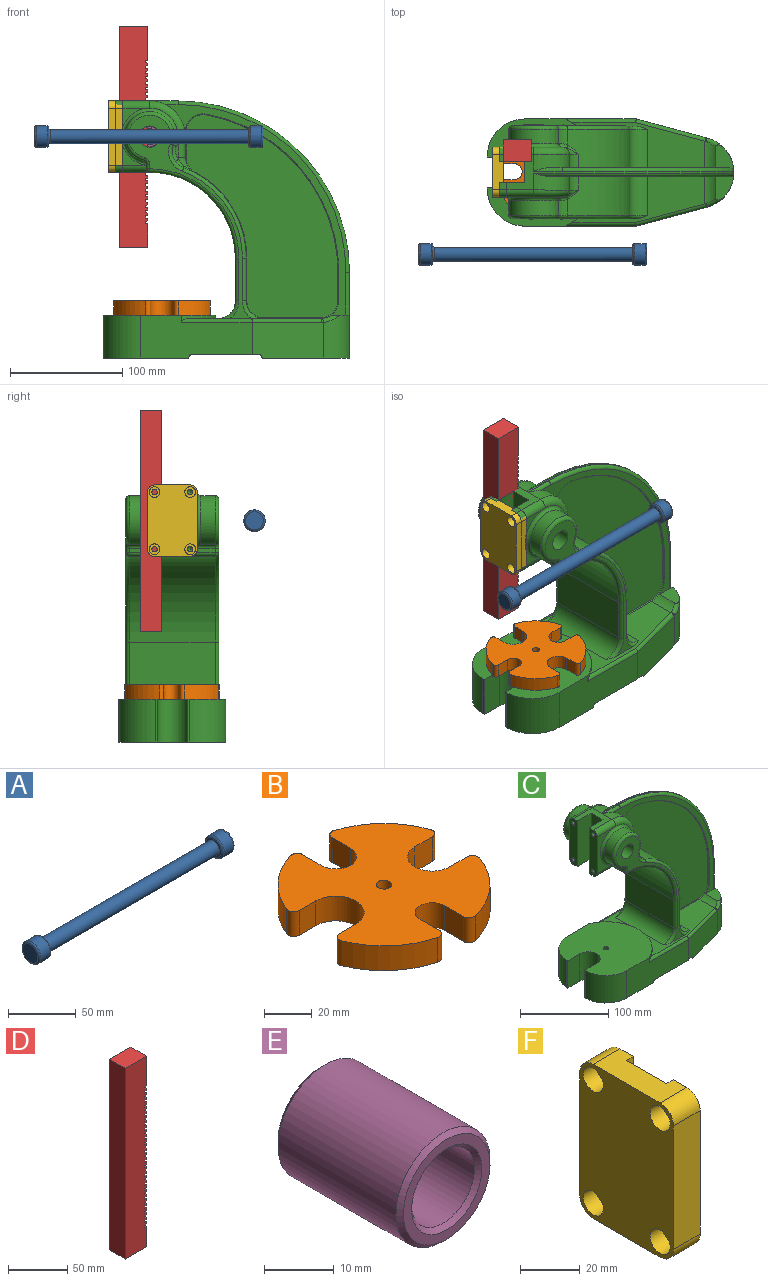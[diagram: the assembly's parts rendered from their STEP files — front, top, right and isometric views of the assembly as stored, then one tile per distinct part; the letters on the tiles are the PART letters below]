
ASSEMBLY  parts=6 mates=1
PART A: 12 faces, bbox 203.2x20.6x20.6 mm
  f0: cylinder r=6.1mm len=176.28mm, axis (-1,0,0), area 6751.8mm2, adj f5,f7
  f1: cylinder r=9.53mm len=19.05mm, axis (-1,0,0), area 577.6mm2, adj f10,f11
  f2: plane 16x16mm, normal (1,0,0), area 18.7mm2, adj f7,f11
  f3: plane 16x16mm, normal (-1,0,0), area 201.1mm2, adj f10
  f4: cylinder r=9.53mm len=19.05mm, axis (1,0,0), area 577.6mm2, adj f8,f9
  f5: plane 16x16mm, normal (-1,0,0), area 84.4mm2, adj f0,f9
  f6: plane 16x16mm, normal (1,0,0), area 201.1mm2, adj f8
  f7: torus R=7.62mm, axis (-1,0,0), area 100mm2, adj f0,f2
  f8: torus R=8mm, axis (1,0,0), area 134.9mm2, adj f4,f6
  f9: torus R=8mm, axis (1,0,0), area 134.9mm2, adj f4,f5
  f10: torus R=8mm, axis (1,0,0), area 134.9mm2, adj f1,f3
  f11: torus R=8mm, axis (-1,0,0), area 134.9mm2, adj f1,f2
PART B: 27 faces, bbox 83.8x85.8x12.7 mm
  f0: cylinder r=44.45mm len=28.56mm, axis (0,0,-1), area 510.6mm2, adj f17,f18,f19,f25
  f1: plane 12.7x9.85mm, normal (0,-1,0), area 125.1mm2, adj f2,f17,f18,f25
  f2: cylinder r=11.9mm len=23.8mm, axis (0,0,-1), area 474.8mm2, adj f1,f3,f17,f18
  f3: plane 12.7x9.85mm, normal (0,1,0), area 125.1mm2, adj f2,f17,f18,f26
  f4: cylinder r=44.45mm len=30.27mm, axis (0,0,-1), area 533.1mm2, adj f17,f18,f20,f26
  f5: plane 12.7x11.39mm, normal (1,0,0), area 144.7mm2, adj f6,f17,f18,f20
  f6: cylinder r=7.14mm len=14.28mm, axis (0,0,-1), area 284.8mm2, adj f5,f7,f17,f18
  f7: plane 12.7x11.39mm, normal (-1,0,0), area 144.7mm2, adj f6,f17,f18,f21
  f8: cylinder r=44.45mm len=30.9mm, axis (0,0,-1), area 556.3mm2, adj f17,f18,f21,f22
  f9: plane 12.7x10.43mm, normal (0,1,0), area 132.5mm2, adj f10,f17,f18,f22
  f10: cylinder r=10.31mm len=20.62mm, axis (0,0,-1), area 411.4mm2, adj f9,f11,f17,f18
  f11: plane 12.7x10.43mm, normal (0,-1,0), area 132.5mm2, adj f10,f17,f18,f23
  f12: cylinder r=44.45mm len=29.19mm, axis (0,0,-1), area 533.7mm2, adj f17,f18,f23,f24
  f13: plane 12.7x10.95mm, normal (-1,0,0), area 139mm2, adj f14,f17,f18,f24
  f14: cylinder r=8.72mm len=17.45mm, axis (0,0,-1), area 348.1mm2, adj f13,f15,f17,f18
  f15: plane 12.7x10.95mm, normal (1,0,0), area 139mm2, adj f14,f17,f18,f19
  f16: cylinder r=3.17mm len=12.7mm, axis (0,0,-1), area 253.4mm2, adj f17,f18
  f17: plane 85.84x83.78mm, normal (0,0,1), area 4373.8mm2, adj f0,f1,f2,f3,f4,f5,f6,f7
  f18: plane 85.84x83.78mm, normal (0,0,-1), area 4373.8mm2, adj f0,f1,f2,f3,f4,f5,f6,f7
  f19: cylinder r=3.17mm len=12.7mm, axis (0,0,-1), area 75.1mm2, adj f0,f15,f17,f18
  f20: cylinder r=3.17mm len=12.7mm, axis (0,0,-1), area 73.5mm2, adj f4,f5,f17,f18
  f21: cylinder r=3.17mm len=12.7mm, axis (0,0,-1), area 73.5mm2, adj f7,f8,f17,f18
  f22: cylinder r=3.17mm len=12.7mm, axis (0,0,-1), area 76.8mm2, adj f8,f9,f17,f18
  f23: cylinder r=3.17mm len=12.7mm, axis (0,0,-1), area 76.8mm2, adj f11,f12,f17,f18
  f24: cylinder r=3.17mm len=12.7mm, axis (0,0,-1), area 75.1mm2, adj f12,f13,f17,f18
  f25: cylinder r=3.17mm len=12.7mm, axis (0,0,-1), area 78.4mm2, adj f0,f1,f17,f18
  f26: cylinder r=3.17mm len=12.7mm, axis (0,0,-1), area 78.4mm2, adj f3,f4,f17,f18
PART C: 180 faces, bbox 234.5x98.1x244 mm
  f0: plane 63.5x12.7mm, normal (-1,0,0), area 753.5mm2, adj f2,f15,f17,f92,f97,f149,f151,f158
  f1: plane 20.23x2.34mm, normal (0,1,0), area 23.9mm2, adj f90,f91,f104,f106
  f2: plane 50.8x30.1mm, normal (0,-1,0), area 515.4mm2, adj f0,f83,f92,f97,f124
  f3: plane 22.59x12.73mm, normal (1,0,0), area 235.4mm2, adj f19,f26,f32,f87,f94,f174
  f4: plane 22.59x12.73mm, normal (1,0,0), area 235.4mm2, adj f10,f14,f33,f86,f90,f164
  f5: plane 99.19x38.1mm, normal (0,-1,0), area 3202mm2, adj f6,f40,f46,f49,f52,f58,f76,f133
  f6: plane 100x95.25mm, normal (0,0,1), area 7398mm2, adj f5,f43,f44,f48,f54,f55,f56,f57
  f7: plane 38.1x34.96mm, normal (1,0,0), area 1331.9mm2, adj f8,f9,f114,f169
  f8: cylinder r=15.88mm len=34.96mm, axis (0,1,0), area 871.7mm2, adj f7,f37,f115,f167
  f9: cylinder r=85.72mm len=80.21mm, axis (0,1,0), area 3442.3mm2, adj f7,f80,f86,f100,f113,f168
  f10: cylinder r=15.88mm len=18.65mm, axis (0,1,0), area 22.7mm2, adj f4,f11,f33,f162
  f11: cylinder r=142.88mm len=140.67mm, axis (0,1,0), area 163.3mm2, adj f10,f12,f33,f160
  f12: plane 25.4x0.82mm, normal (-1,0,0), area 20.8mm2, adj f11,f13,f33,f161
  f13: cylinder r=15.88mm len=24.81mm, axis (0,1,0), area 242.1mm2, adj f12,f33,f37,f45,f139,f140,f163
  f14: cylinder r=31.75mm len=31.75mm, axis (0,1,0), area 616.8mm2, adj f4,f15,f33,f89,f141
  f15: plane 55.5x31.75mm, normal (0,0,1), area 573.2mm2, adj f0,f14,f16,f19,f31,f88,f92,f141
  f16: plane 63.5x12.7mm, normal (-1,0,0), area 753.5mm2, adj f15,f17,f21,f88,f96,f147,f153,f157
  f17: plane 31.75x30.1mm, normal (0,0,-1), area 533.2mm2, adj f0,f16,f18,f96,f97,f156,f157,f158
  f18: cylinder r=76.2mm len=76.2mm, axis (0,1,0), area 9120.7mm2, adj f17,f22,f103,f105,f119,f121
  f19: cylinder r=31.75mm len=31.75mm, axis (0,1,0), area 616.8mm2, adj f3,f15,f32,f93,f144
  f20: plane 20.23x2.34mm, normal (0,-1,0), area 23.9mm2, adj f94,f95,f122,f124
  f21: plane 50.8x30.1mm, normal (0,1,0), area 515.4mm2, adj f16,f78,f88,f96,f106
  f22: plane 76.2x38.1mm, normal (-1,0,0), area 2903.2mm2, adj f18,f98,f101,f117
  f23: cylinder r=15.88mm len=34.96mm, axis (0,1,0), area 871.7mm2, adj f24,f37,f132,f177
  f24: plane 38.1x34.96mm, normal (1,0,0), area 1331.9mm2, adj f23,f25,f131,f179
  f25: cylinder r=85.72mm len=80.21mm, axis (0,1,0), area 3442.3mm2, adj f24,f81,f87,f118,f130,f178
  f26: cylinder r=15.88mm len=18.65mm, axis (0,1,0), area 22.7mm2, adj f3,f27,f32,f172
  f27: cylinder r=142.88mm len=140.67mm, axis (0,1,0), area 163.3mm2, adj f26,f28,f32,f170
  f28: plane 25.4x0.82mm, normal (-1,0,0), area 20.8mm2, adj f27,f29,f32,f171
  f29: cylinder r=15.88mm len=24.81mm, axis (0,1,0), area 242.1mm2, adj f28,f32,f36,f37,f135,f136,f173
  f30: plane 76.2x7.92mm, normal (1,0,0), area 361.9mm2, adj f31,f36,f42,f45,f51,f53,f143,f146
  f31: cylinder r=152.4mm len=152.4mm, axis (0,1,0), area 377mm2, adj f15,f30,f142,f145
  f32: plane 187.33x160.79mm, normal (0,-1,0), area 1900.4mm2, adj f3,f19,f26,f27,f28,f29,f36,f144
  f33: plane 187.33x160.79mm, normal (0,1,0), area 1900.4mm2, adj f4,f10,f11,f12,f13,f14,f45,f141
  f34: plane 180.67x135mm, normal (0,-1,0), area 14138.8mm2, adj f170,f171,f172,f173,f174,f175,f176,f177
  f35: plane 180.67x135mm, normal (0,1,0), area 14138.8mm2, adj f160,f161,f162,f163,f164,f165,f166,f167
  f36: plane 26.58x18.73mm, normal (0,0,1), area 245.8mm2, adj f29,f30,f32,f53,f136,f146
  f37: plane 119.12x89.67mm, normal (0,0,1), area 4280.2mm2, adj f8,f13,f23,f29,f76,f77,f84,f98
  f38: cylinder r=3.17mm len=9.06mm, axis (0,1,0), area 40.9mm2, adj f40,f42,f52,f69
  f39: cylinder r=3.17mm len=7.93mm, axis (0,1,0), area 39.5mm2, adj f41,f46,f48,f65
  f40: plane 58.73x9.7mm, normal (0,0,-1), area 467.1mm2, adj f5,f38,f49,f52,f64,f69
  f41: plane 58.73x9.7mm, normal (0,0,-1), area 467.1mm2, adj f39,f47,f48,f50,f65,f67
  f42: plane 90.55x77.8mm, normal (0,0,-1), area 1454mm2, adj f30,f38,f47,f50,f51,f52,f53,f59
  f43: plane 38.1x1.61mm, normal (-1,0,0), area 61.5mm2, adj f6,f46,f54,f58
  f44: plane 38.1x1.61mm, normal (-1,0,0), area 61.5mm2, adj f6,f46,f55,f57
  f45: plane 26.58x18.73mm, normal (0,0,1), area 245.8mm2, adj f13,f30,f33,f51,f140,f143
  f46: plane 95.25x76.2mm, normal (0,0,-1), area 2029.8mm2, adj f5,f39,f43,f44,f48,f49,f54,f55
  f47: cylinder r=3.17mm len=9.06mm, axis (0,1,0), area 40.9mm2, adj f41,f42,f50,f67
  f48: plane 99.19x38.1mm, normal (0,1,0), area 3202mm2, adj f6,f39,f41,f46,f50,f57,f76,f137
  f49: cylinder r=3.17mm len=7.93mm, axis (0,1,0), area 39.5mm2, adj f5,f40,f46,f64
  f50: plane 63.64x32.15mm, normal (0.26,0.97,0), area 2053.6mm2, adj f41,f42,f47,f48,f51,f138,f139
  f51: cylinder r=31.75mm len=38.1mm, axis (0,0,-1), area 1379.2mm2, adj f30,f42,f45,f50,f140
  f52: plane 63.64x32.15mm, normal (0.26,-0.97,0), area 2053.6mm2, adj f5,f38,f40,f42,f53,f134,f135
  f53: cylinder r=31.75mm len=38.1mm, axis (0,0,-1), area 1379.2mm2, adj f30,f36,f42,f52,f136
  f54: plane 38.1x19.05mm, normal (0,1,0), area 725.8mm2, adj f6,f43,f46,f56
  f55: plane 38.1x19.05mm, normal (0,-1,0), area 725.8mm2, adj f6,f44,f46,f56
  f56: cylinder r=13.49mm len=38.1mm, axis (0,0,-1), area 1615.1mm2, adj f6,f46,f54,f55
  f57: cylinder r=33.32mm len=38.1mm, axis (0,0,-1), area 1963.7mm2, adj f6,f44,f46,f48
  f58: cylinder r=33.32mm len=38.1mm, axis (0,0,-1), area 1963.7mm2, adj f5,f6,f43,f46
  f59: plane 30.18x6.86mm, normal (-1,0,0), area 207mm2, adj f42,f60,f68,f70
  f60: plane 31.27x5.6mm, normal (0,0,-1), area 124.1mm2, adj f59,f61,f68,f70
  f61: cylinder r=23.8mm len=46.06mm, axis (0,1,0), area 499.2mm2, adj f60,f62,f67,f68,f69,f70
  f62: plane 84.13x79.4mm, normal (0,0,-1), area 5642.5mm2, adj f61,f64,f65,f66,f67,f69
  f63: plane 100.62x79.4mm, normal (0,0,-1), area 6568.5mm2, adj f64,f65,f66,f71,f72,f73,f74,f75
  f64: plane 98.15x30.18mm, normal (0,1,0), area 2718.8mm2, adj f40,f46,f49,f62,f63,f66,f69,f75
  f65: plane 98.15x30.18mm, normal (0,-1,0), area 2718.8mm2, adj f39,f41,f46,f62,f63,f66,f67,f74
  f66: plane 79.4x3.18mm, normal (-1,0,0), area 252.1mm2, adj f62,f63,f64,f65
  f67: plane 62.63x27.36mm, normal (-0.26,-0.97,0), area 1710.8mm2, adj f41,f42,f47,f61,f62,f65,f68
  f68: cylinder r=23.83mm len=30.18mm, axis (0,0,-1), area 814.8mm2, adj f42,f59,f60,f61,f67
  f69: plane 62.63x27.36mm, normal (-0.26,0.97,0), area 1710.8mm2, adj f38,f40,f42,f61,f62,f64,f70
  f70: cylinder r=23.83mm len=30.18mm, axis (0,0,-1), area 814.8mm2, adj f42,f59,f60,f61,f69
  f71: plane 30.18x10.12mm, normal (0,-1,0), area 305.3mm2, adj f46,f63,f73,f75
  f72: plane 30.18x10.12mm, normal (0,1,0), area 305.3mm2, adj f46,f63,f73,f74
  f73: cylinder r=21.42mm len=42.84mm, axis (0,0,-1), area 2030.4mm2, adj f46,f63,f71,f72
  f74: cylinder r=25.4mm len=30.18mm, axis (0,0,-1), area 986.2mm2, adj f46,f63,f65,f72
  f75: cylinder r=25.4mm len=30.18mm, axis (0,0,-1), area 986.2mm2, adj f46,f63,f64,f71
  f76: cylinder r=52.37mm len=95.25mm, axis (0,0,1), area 401mm2, adj f5,f6,f37,f48,f133,f137
  f77: plane 180.98x110.12mm, normal (0,1,0), area 1717.8mm2, adj f37,f85,f99,f101,f103,f109,f110,f111
  f78: plane 16.73x3.98mm, normal (-1,0,0), area 64.1mm2, adj f21,f96,f105,f106,f108,f109
  f79: cylinder r=22.23mm len=44.45mm, axis (0,1,0), area 1356.2mm2, adj f80,f106,f108,f111
  f80: cylinder r=15.88mm len=20.22mm, axis (0,1,0), area 319.4mm2, adj f9,f79,f102,f104,f112
  f81: cylinder r=15.88mm len=20.22mm, axis (0,1,0), area 319.4mm2, adj f25,f82,f120,f122,f129
  f82: cylinder r=22.23mm len=44.45mm, axis (0,1,0), area 1356.2mm2, adj f81,f124,f126,f128
  f83: plane 16.73x3.98mm, normal (-1,0,0), area 64.1mm2, adj f2,f97,f121,f124,f125,f126
  f84: plane 180.98x110.12mm, normal (0,-1,0), area 1717.8mm2, adj f37,f85,f116,f117,f119,f125,f127,f128
  f85: cylinder r=9.53mm len=82.55mm, axis (0,1,0), area 4727mm2, adj f77,f84,f156,f157,f158,f159
  f86: cylinder r=15.88mm len=14.02mm, axis (0,1,0), area 218.9mm2, adj f4,f9,f91,f166
  f87: cylinder r=15.88mm len=14.02mm, axis (0,1,0), area 218.9mm2, adj f3,f25,f95,f176
  f88: cylinder r=6.35mm len=30.1mm, axis (-1,0,0), area 300.2mm2, adj f15,f16,f21,f89
  f89: torus R=25.4mm, axis (0,-1,0), area 461.3mm2, adj f14,f88,f90,f106
  f90: cylinder r=6.35mm len=18.2mm, axis (0,0,1), area 181.6mm2, adj f1,f4,f89,f91
  f91: torus R=22.23mm, axis (0,-1,0), area 98mm2, adj f1,f86,f90,f100,f102
  f92: cylinder r=6.35mm len=30.1mm, axis (1,0,0), area 300.2mm2, adj f0,f2,f15,f93
  f93: torus R=25.4mm, axis (0,-1,0), area 461.3mm2, adj f19,f92,f94,f124
  f94: cylinder r=6.35mm len=18.2mm, axis (0,0,-1), area 181.6mm2, adj f3,f20,f93,f95
  f95: torus R=22.23mm, axis (0,-1,0), area 98mm2, adj f20,f87,f94,f118,f120
  f96: cylinder r=6.35mm len=30.1mm, axis (1,0,0), area 279.1mm2, adj f16,f17,f21,f78,f105
  f97: cylinder r=6.35mm len=30.1mm, axis (-1,0,0), area 279.1mm2, adj f0,f2,f17,f83,f121
  f98: cylinder r=15.88mm len=76.2mm, axis (0,-1,0), area 1900.2mm2, adj f22,f37,f99,f116
  f99: torus R=19.05mm, axis (0,-1,0), area 107.7mm2, adj f37,f77,f98,f101
  f100: bspline ~12.01x8.85mm, area 17.9mm2, adj f9,f91,f102
  f101: cylinder r=3.17mm len=38.1mm, axis (0,0,-1), area 190mm2, adj f22,f77,f99,f103
  f102: bspline ~10.6x9.56mm, area 36.6mm2, adj f80,f91,f100,f104
  f103: torus R=79.38mm, axis (0,-1,0), area 606mm2, adj f18,f77,f101,f107
  f104: torus R=12.7mm, axis (0,-1,0), area 70.6mm2, adj f1,f80,f102,f106
  f105: cylinder r=3.17mm len=22.23mm, axis (0,1,0), area 97.1mm2, adj f18,f78,f96,f107
  f106: torus R=25.4mm, axis (0,-1,0), area 570mm2, adj f1,f21,f78,f79,f89,f104,f108
  f107: sphere r=3.17mm, area 21.6mm2, adj f103,f105,f109
  f108: cylinder r=3.17mm len=15.82mm, axis (0,1,0), area 59.7mm2, adj f78,f79,f106,f110
  f109: cylinder r=3.17mm len=3.98mm, axis (0,0,-1), area 19.9mm2, adj f77,f78,f107,f110
  f110: torus R=6.35mm, axis (0,-1,0), area 28.5mm2, adj f77,f108,f109,f111
  f111: torus R=19.05mm, axis (0,-1,0), area 504.9mm2, adj f77,f79,f110,f112
  f112: torus R=19.05mm, axis (0,-1,0), area 132.1mm2, adj f77,f80,f111,f113
  f113: torus R=82.55mm, axis (0,-1,0), area 510.4mm2, adj f9,f77,f112,f114
  f114: cylinder r=3.17mm len=38.1mm, axis (0,0,1), area 190mm2, adj f7,f77,f113,f115
  f115: torus R=19.05mm, axis (0,-1,0), area 107.7mm2, adj f8,f37,f77,f114
  f116: torus R=19.05mm, axis (0,-1,0), area 107.7mm2, adj f37,f84,f98,f117
  f117: cylinder r=3.17mm len=38.1mm, axis (0,0,1), area 190mm2, adj f22,f84,f116,f119
  f118: bspline ~11.06x8.44mm, area 17.9mm2, adj f25,f95,f120
  f119: torus R=79.38mm, axis (0,-1,0), area 606mm2, adj f18,f84,f117,f123
  f120: bspline ~9.12x8.99mm, area 36.6mm2, adj f81,f95,f118,f122
  f121: cylinder r=3.17mm len=22.23mm, axis (0,1,0), area 97.1mm2, adj f18,f83,f97,f123
  f122: torus R=12.7mm, axis (0,-1,0), area 70.6mm2, adj f20,f81,f120,f124
  f123: sphere r=3.17mm, area 15.8mm2, adj f119,f121,f125
  f124: torus R=25.4mm, axis (0,-1,0), area 570mm2, adj f2,f20,f82,f83,f93,f122,f126
  f125: cylinder r=3.17mm len=3.98mm, axis (0,0,1), area 19.9mm2, adj f83,f84,f123,f127
  f126: cylinder r=3.17mm len=15.82mm, axis (0,1,0), area 59.7mm2, adj f82,f83,f124,f127
  f127: torus R=6.35mm, axis (0,-1,0), area 28.5mm2, adj f84,f125,f126,f128
  f128: torus R=19.05mm, axis (0,-1,0), area 504.9mm2, adj f82,f84,f127,f129
  f129: torus R=19.05mm, axis (0,-1,0), area 132.1mm2, adj f81,f84,f128,f130
  f130: torus R=82.55mm, axis (0,-1,0), area 510.4mm2, adj f25,f84,f129,f131
  f131: cylinder r=3.17mm len=38.1mm, axis (0,0,-1), area 190mm2, adj f24,f84,f130,f132
  f132: torus R=19.05mm, axis (0,-1,0), area 107.7mm2, adj f23,f37,f84,f131
  f133: cylinder r=3.17mm len=63.09mm, axis (1,0,0), area 298.9mm2, adj f5,f37,f76,f134
  f134: cylinder r=3.17mm len=62.81mm, axis (0.97,0.26,0), area 319mm2, adj f37,f52,f133,f135
  f135: bspline ~3.41x3.21mm, area 6mm2, adj f29,f52,f134,f136
  f136: bspline ~18.95x11.92mm, area 79.7mm2, adj f29,f36,f53,f135
  f137: cylinder r=3.17mm len=63.09mm, axis (-1,0,0), area 298.9mm2, adj f37,f48,f76,f138
  f138: cylinder r=3.17mm len=62.81mm, axis (-0.97,0.26,0), area 319mm2, adj f37,f50,f137,f139
  f139: bspline ~6.89x4.84mm, area 6mm2, adj f13,f50,f138,f140
  f140: bspline ~17.46x11.57mm, area 79.7mm2, adj f13,f45,f51,f139
  f141: cylinder r=3.17mm len=25.4mm, axis (-1,0,0), area 92.2mm2, adj f14,f15,f33,f142
  f142: torus R=149.22mm, axis (0,-1,0), area 1184.9mm2, adj f31,f33,f141,f143
  f143: cylinder r=3.17mm len=38.1mm, axis (0,0,1), area 190mm2, adj f30,f33,f45,f142
  f144: cylinder r=3.17mm len=25.4mm, axis (1,0,0), area 92.2mm2, adj f15,f19,f32,f145
  f145: torus R=149.22mm, axis (0,-1,0), area 1184.9mm2, adj f31,f32,f144,f146
  f146: cylinder r=3.17mm len=38.1mm, axis (0,0,-1), area 190mm2, adj f30,f32,f36,f145
  f147: cylinder r=2.38mm len=6.35mm, axis (-1,0,0), area 95mm2, adj f16,f148
  f148: cone r=0mm half-angle=59deg, axis (-1,0,0), area 20.8mm2, adj f147
  f149: cylinder r=2.38mm len=6.35mm, axis (-1,0,0), area 95mm2, adj f0,f150
  f150: cone r=0mm half-angle=59deg, axis (-1,0,0), area 20.8mm2, adj f149
  f151: cylinder r=2.38mm len=6.35mm, axis (-1,0,0), area 95mm2, adj f0,f152
  f152: cone r=0mm half-angle=59deg, axis (-1,0,0), area 20.8mm2, adj f151
  f153: cylinder r=2.38mm len=6.35mm, axis (-1,0,0), area 95mm2, adj f16,f154
  f154: cone r=0mm half-angle=59deg, axis (-1,0,0), area 20.8mm2, adj f153
  f155: cylinder r=3.17mm len=7.93mm, axis (0,0,1), area 158.1mm2, adj f6,f63
  f156: plane 26.47x19.05mm, normal (-1,0,0), area 504.2mm2, adj f17,f85,f157,f158
  f157: plane 63.5x22.17mm, normal (0,-1,0), area 1396.6mm2, adj f15,f16,f17,f85,f156,f159
  f158: plane 63.5x22.17mm, normal (0,1,0), area 1396.6mm2, adj f0,f15,f17,f85,f156,f159
  f159: plane 26.47x19.05mm, normal (-1,0,0), area 504.2mm2, adj f15,f85,f157,f158
  f160: torus R=142.11mm, axis (0,-1,0), area 238.1mm2, adj f11,f35,f161,f162
  f161: cylinder r=0.76mm len=25.4mm, axis (0,0,1), area 30.4mm2, adj f12,f35,f160,f163
  f162: torus R=15.11mm, axis (0,-1,0), area 32.6mm2, adj f10,f35,f160,f164
  f163: torus R=15.11mm, axis (0,-1,0), area 29.3mm2, adj f13,f35,f161,f165
  f164: cylinder r=0.76mm len=22.59mm, axis (0,0,1), area 27mm2, adj f4,f35,f162,f166
  f165: cylinder r=0.76mm len=50.8mm, axis (1,0,0), area 60.8mm2, adj f35,f37,f163,f167
  f166: torus R=15.11mm, axis (0,-1,0), area 20.2mm2, adj f35,f86,f164,f168
  f167: torus R=15.11mm, axis (0,-1,0), area 29.3mm2, adj f8,f35,f165,f169
  f168: torus R=86.49mm, axis (0,-1,0), area 111.5mm2, adj f9,f35,f166,f169
  f169: cylinder r=0.76mm len=38.1mm, axis (0,0,-1), area 45.6mm2, adj f7,f35,f167,f168
  f170: torus R=142.11mm, axis (0,-1,0), area 238.1mm2, adj f27,f34,f171,f172
  f171: cylinder r=0.76mm len=25.4mm, axis (0,0,-1), area 30.4mm2, adj f28,f34,f170,f173
  f172: torus R=15.11mm, axis (0,-1,0), area 32.6mm2, adj f26,f34,f170,f174
  f173: torus R=15.11mm, axis (0,-1,0), area 29.3mm2, adj f29,f34,f171,f175
  f174: cylinder r=0.76mm len=22.59mm, axis (0,0,-1), area 27mm2, adj f3,f34,f172,f176
  f175: cylinder r=0.76mm len=50.8mm, axis (-1,0,0), area 60.8mm2, adj f34,f37,f173,f177
  f176: torus R=15.11mm, axis (0,-1,0), area 20.2mm2, adj f34,f87,f174,f178
  f177: torus R=15.11mm, axis (0,-1,0), area 29.3mm2, adj f23,f34,f175,f179
  f178: torus R=86.49mm, axis (0,-1,0), area 111.5mm2, adj f25,f34,f176,f179
  f179: cylinder r=0.76mm len=38.1mm, axis (0,0,1), area 45.6mm2, adj f24,f34,f177,f178
PART D: 130 faces, bbox 25.4x19.1x196.9 mm
  f0: plane 19.05x2.22mm, normal (1,0,0), area 42.3mm2, adj f31,f32,f62,f127
  f1: plane 19.05x2.22mm, normal (1,0,0), area 42.3mm2, adj f31,f32,f124,f128
  f2: plane 19.05x2.22mm, normal (1,0,0), area 42.3mm2, adj f31,f32,f121,f125
  f3: plane 19.05x2.22mm, normal (1,0,0), area 42.3mm2, adj f31,f32,f118,f122
  f4: plane 19.05x2.22mm, normal (1,0,0), area 42.3mm2, adj f31,f32,f115,f119
  f5: plane 19.05x2.22mm, normal (1,0,0), area 42.3mm2, adj f31,f32,f112,f116
  f6: plane 19.05x2.22mm, normal (1,0,0), area 42.3mm2, adj f31,f32,f109,f113
  f7: plane 19.05x2.22mm, normal (1,0,0), area 42.3mm2, adj f31,f32,f104,f106
  f8: plane 19.05x2.22mm, normal (1,0,0), area 42.3mm2, adj f31,f32,f101,f103
  f9: plane 19.05x2.22mm, normal (1,0,0), area 42.3mm2, adj f31,f32,f98,f100
  f10: plane 19.05x2.22mm, normal (1,0,0), area 42.3mm2, adj f31,f32,f95,f97
  f11: plane 19.05x2.22mm, normal (1,0,0), area 42.3mm2, adj f31,f32,f92,f94
  f12: plane 19.05x2.22mm, normal (1,0,0), area 42.3mm2, adj f31,f32,f89,f91
  f13: plane 19.05x2.22mm, normal (1,0,0), area 42.3mm2, adj f31,f32,f86,f88
  f14: plane 19.05x2.22mm, normal (1,0,0), area 42.3mm2, adj f31,f32,f83,f85
  f15: plane 19.05x2.22mm, normal (1,0,0), area 42.3mm2, adj f31,f32,f37,f82
  f16: plane 20.96x19.05mm, normal (1,0,0), area 399.2mm2, adj f31,f32,f36,f79
  f17: plane 19.05x2.22mm, normal (1,0,0), area 42.3mm2, adj f31,f32,f76,f80
  f18: plane 19.05x2.22mm, normal (1,0,0), area 42.3mm2, adj f31,f32,f71,f73
  f19: plane 19.05x2.22mm, normal (1,0,0), area 42.3mm2, adj f31,f32,f68,f70
  f20: plane 19.05x2.22mm, normal (1,0,0), area 42.3mm2, adj f31,f32,f65,f67
  f21: plane 19.05x2.22mm, normal (1,0,0), area 42.3mm2, adj f31,f32,f50,f64
  f22: plane 19.05x2.22mm, normal (1,0,0), area 42.3mm2, adj f31,f32,f59,f61
  f23: plane 19.05x2.22mm, normal (1,0,0), area 42.3mm2, adj f31,f32,f56,f58
  f24: plane 19.05x2.22mm, normal (1,0,0), area 42.3mm2, adj f31,f32,f53,f55
  f25: plane 19.05x2.22mm, normal (1,0,0), area 42.3mm2, adj f31,f32,f41,f52
  f26: plane 19.05x2.22mm, normal (1,0,0), area 42.3mm2, adj f31,f32,f49,f107
  f27: plane 19.05x2.22mm, normal (1,0,0), area 42.3mm2, adj f31,f32,f46,f77
  f28: plane 19.05x2.22mm, normal (1,0,0), area 42.3mm2, adj f31,f32,f43,f47
  f29: plane 19.05x2.22mm, normal (1,0,0), area 42.3mm2, adj f31,f32,f40,f44
  f30: plane 19.05x2.22mm, normal (1,0,0), area 42.3mm2, adj f31,f32,f39,f110
  f31: plane 196.85x25.4mm, normal (0,1,0), area 4862.6mm2, adj f0,f1,f2,f3,f4,f5,f6,f7
  f32: plane 196.85x25.4mm, normal (0,-1,0), area 4862.6mm2, adj f0,f1,f2,f3,f4,f5,f6,f7
  f33: plane 196.85x19.05mm, normal (-1,0,0), area 3750mm2, adj f31,f32,f35,f36
  f34: plane 30.48x19.05mm, normal (1,0,0), area 580.6mm2, adj f31,f32,f35,f74
  f35: plane 25.4x19.05mm, normal (0,0,1), area 483.9mm2, adj f31,f32,f33,f34
  f36: plane 25.4x19.05mm, normal (0,0,-1), area 483.9mm2, adj f16,f31,f32,f33
  f37: plane 19.05x2.03mm, normal (0.17,0,-0.98), area 39.3mm2, adj f15,f31,f32,f38
  f38: plane 19.05x1.82mm, normal (1,0,0), area 34.7mm2, adj f31,f32,f37,f39
  f39: plane 19.05x2.03mm, normal (0.17,0,0.98), area 39.3mm2, adj f30,f31,f32,f38
  f40: plane 19.05x2.03mm, normal (0.17,0,0.98), area 39.3mm2, adj f29,f31,f32,f42
  f41: plane 19.05x2.03mm, normal (0.17,0,-0.98), area 39.3mm2, adj f25,f31,f32,f42
  f42: plane 19.05x1.82mm, normal (1,0,0), area 34.7mm2, adj f31,f32,f40,f41
  f43: plane 19.05x2.03mm, normal (0.17,0,0.98), area 39.3mm2, adj f28,f31,f32,f45
  f44: plane 19.05x2.03mm, normal (0.17,0,-0.98), area 39.3mm2, adj f29,f31,f32,f45
  f45: plane 19.05x1.82mm, normal (1,0,0), area 34.7mm2, adj f31,f32,f43,f44
  f46: plane 19.05x2.03mm, normal (0.17,0,0.98), area 39.3mm2, adj f27,f31,f32,f48
  f47: plane 19.05x2.03mm, normal (0.17,0,-0.98), area 39.3mm2, adj f28,f31,f32,f48
  f48: plane 19.05x1.82mm, normal (1,0,0), area 34.7mm2, adj f31,f32,f46,f47
  f49: plane 19.05x2.03mm, normal (0.17,0,0.98), area 39.3mm2, adj f26,f31,f32,f51
  f50: plane 19.05x2.03mm, normal (0.17,0,-0.98), area 39.3mm2, adj f21,f31,f32,f51
  f51: plane 19.05x1.82mm, normal (1,0,0), area 34.7mm2, adj f31,f32,f49,f50
  f52: plane 19.05x2.03mm, normal (0.17,0,0.98), area 39.3mm2, adj f25,f31,f32,f54
  f53: plane 19.05x2.03mm, normal (0.17,0,-0.98), area 39.3mm2, adj f24,f31,f32,f54
  f54: plane 19.05x1.82mm, normal (1,0,0), area 34.7mm2, adj f31,f32,f52,f53
  f55: plane 19.05x2.03mm, normal (0.17,0,0.98), area 39.3mm2, adj f24,f31,f32,f57
  f56: plane 19.05x2.03mm, normal (0.17,0,-0.98), area 39.3mm2, adj f23,f31,f32,f57
  f57: plane 19.05x1.82mm, normal (1,0,0), area 34.7mm2, adj f31,f32,f55,f56
  f58: plane 19.05x2.03mm, normal (0.17,0,0.98), area 39.3mm2, adj f23,f31,f32,f60
  f59: plane 19.05x2.03mm, normal (0.17,0,-0.98), area 39.3mm2, adj f22,f31,f32,f60
  f60: plane 19.05x1.82mm, normal (1,0,0), area 34.7mm2, adj f31,f32,f58,f59
  f61: plane 19.05x2.03mm, normal (0.17,0,0.98), area 39.3mm2, adj f22,f31,f32,f63
  f62: plane 19.05x2.03mm, normal (0.17,0,-0.98), area 39.3mm2, adj f0,f31,f32,f63
  f63: plane 19.05x1.82mm, normal (1,0,0), area 34.7mm2, adj f31,f32,f61,f62
  f64: plane 19.05x2.03mm, normal (0.17,0,0.98), area 39.3mm2, adj f21,f31,f32,f66
  f65: plane 19.05x2.03mm, normal (0.17,0,-0.98), area 39.3mm2, adj f20,f31,f32,f66
  f66: plane 19.05x1.82mm, normal (1,0,0), area 34.7mm2, adj f31,f32,f64,f65
  f67: plane 19.05x2.03mm, normal (0.17,0,0.98), area 39.3mm2, adj f20,f31,f32,f69
  f68: plane 19.05x2.03mm, normal (0.17,0,-0.98), area 39.3mm2, adj f19,f31,f32,f69
  f69: plane 19.05x1.82mm, normal (1,0,0), area 34.7mm2, adj f31,f32,f67,f68
  f70: plane 19.05x2.03mm, normal (0.17,0,0.98), area 39.3mm2, adj f19,f31,f32,f72
  f71: plane 19.05x2.03mm, normal (0.17,0,-0.98), area 39.3mm2, adj f18,f31,f32,f72
  f72: plane 19.05x1.82mm, normal (1,0,0), area 34.7mm2, adj f31,f32,f70,f71
  f73: plane 19.05x2.03mm, normal (0.17,0,0.98), area 39.3mm2, adj f18,f31,f32,f75
  f74: plane 19.05x2.03mm, normal (0.17,0,-0.98), area 39.3mm2, adj f31,f32,f34,f75
  f75: plane 19.05x1.82mm, normal (1,0,0), area 34.7mm2, adj f31,f32,f73,f74
  f76: plane 19.05x2.03mm, normal (0.17,0,0.98), area 39.3mm2, adj f17,f31,f32,f78
  f77: plane 19.05x2.03mm, normal (0.17,0,-0.98), area 39.3mm2, adj f27,f31,f32,f78
  f78: plane 19.05x1.82mm, normal (1,0,0), area 34.7mm2, adj f31,f32,f76,f77
  f79: plane 19.05x2.03mm, normal (0.17,0,0.98), area 39.3mm2, adj f16,f31,f32,f81
  f80: plane 19.05x2.03mm, normal (0.17,0,-0.98), area 39.3mm2, adj f17,f31,f32,f81
  f81: plane 19.05x1.82mm, normal (1,0,0), area 34.7mm2, adj f31,f32,f79,f80
  f82: plane 19.05x2.03mm, normal (0.17,0,0.98), area 39.3mm2, adj f15,f31,f32,f84
  f83: plane 19.05x2.03mm, normal (0.17,0,-0.98), area 39.3mm2, adj f14,f31,f32,f84
  f84: plane 19.05x1.82mm, normal (1,0,0), area 34.7mm2, adj f31,f32,f82,f83
  f85: plane 19.05x2.03mm, normal (0.17,0,0.98), area 39.3mm2, adj f14,f31,f32,f87
  f86: plane 19.05x2.03mm, normal (0.17,0,-0.98), area 39.3mm2, adj f13,f31,f32,f87
  f87: plane 19.05x1.82mm, normal (1,0,0), area 34.7mm2, adj f31,f32,f85,f86
  f88: plane 19.05x2.03mm, normal (0.17,0,0.98), area 39.3mm2, adj f13,f31,f32,f90
  f89: plane 19.05x2.03mm, normal (0.17,0,-0.98), area 39.3mm2, adj f12,f31,f32,f90
  f90: plane 19.05x1.82mm, normal (1,0,0), area 34.7mm2, adj f31,f32,f88,f89
  f91: plane 19.05x2.03mm, normal (0.17,0,0.98), area 39.3mm2, adj f12,f31,f32,f93
  f92: plane 19.05x2.03mm, normal (0.17,0,-0.98), area 39.3mm2, adj f11,f31,f32,f93
  f93: plane 19.05x1.82mm, normal (1,0,0), area 34.7mm2, adj f31,f32,f91,f92
  f94: plane 19.05x2.03mm, normal (0.17,0,0.98), area 39.3mm2, adj f11,f31,f32,f96
  f95: plane 19.05x2.03mm, normal (0.17,0,-0.98), area 39.3mm2, adj f10,f31,f32,f96
  f96: plane 19.05x1.82mm, normal (1,0,0), area 34.7mm2, adj f31,f32,f94,f95
  f97: plane 19.05x2.03mm, normal (0.17,0,0.98), area 39.3mm2, adj f10,f31,f32,f99
  f98: plane 19.05x2.03mm, normal (0.17,0,-0.98), area 39.3mm2, adj f9,f31,f32,f99
  f99: plane 19.05x1.82mm, normal (1,0,0), area 34.7mm2, adj f31,f32,f97,f98
  f100: plane 19.05x2.03mm, normal (0.17,0,0.98), area 39.3mm2, adj f9,f31,f32,f102
  f101: plane 19.05x2.03mm, normal (0.17,0,-0.98), area 39.3mm2, adj f8,f31,f32,f102
  f102: plane 19.05x1.82mm, normal (1,0,0), area 34.7mm2, adj f31,f32,f100,f101
  f103: plane 19.05x2.03mm, normal (0.17,0,0.98), area 39.3mm2, adj f8,f31,f32,f105
  f104: plane 19.05x2.03mm, normal (0.17,0,-0.98), area 39.3mm2, adj f7,f31,f32,f105
  f105: plane 19.05x1.82mm, normal (1,0,0), area 34.7mm2, adj f31,f32,f103,f104
  f106: plane 19.05x2.03mm, normal (0.17,0,0.98), area 39.3mm2, adj f7,f31,f32,f108
  f107: plane 19.05x2.03mm, normal (0.17,0,-0.98), area 39.3mm2, adj f26,f31,f32,f108
  f108: plane 19.05x1.82mm, normal (1,0,0), area 34.7mm2, adj f31,f32,f106,f107
  f109: plane 19.05x2.03mm, normal (0.17,0,0.98), area 39.3mm2, adj f6,f31,f32,f111
  f110: plane 19.05x2.03mm, normal (0.17,0,-0.98), area 39.3mm2, adj f30,f31,f32,f111
  f111: plane 19.05x1.82mm, normal (1,0,0), area 34.7mm2, adj f31,f32,f109,f110
  f112: plane 19.05x2.03mm, normal (0.17,0,0.98), area 39.3mm2, adj f5,f31,f32,f114
  f113: plane 19.05x2.03mm, normal (0.17,0,-0.98), area 39.3mm2, adj f6,f31,f32,f114
  f114: plane 19.05x1.82mm, normal (1,0,0), area 34.7mm2, adj f31,f32,f112,f113
  f115: plane 19.05x2.03mm, normal (0.17,0,0.98), area 39.3mm2, adj f4,f31,f32,f117
  f116: plane 19.05x2.03mm, normal (0.17,0,-0.98), area 39.3mm2, adj f5,f31,f32,f117
  f117: plane 19.05x1.82mm, normal (1,0,0), area 34.7mm2, adj f31,f32,f115,f116
  f118: plane 19.05x2.03mm, normal (0.17,0,0.98), area 39.3mm2, adj f3,f31,f32,f120
  f119: plane 19.05x2.03mm, normal (0.17,0,-0.98), area 39.3mm2, adj f4,f31,f32,f120
  f120: plane 19.05x1.82mm, normal (1,0,0), area 34.7mm2, adj f31,f32,f118,f119
  f121: plane 19.05x2.03mm, normal (0.17,0,0.98), area 39.3mm2, adj f2,f31,f32,f123
  f122: plane 19.05x2.03mm, normal (0.17,0,-0.98), area 39.3mm2, adj f3,f31,f32,f123
  f123: plane 19.05x1.82mm, normal (1,0,0), area 34.7mm2, adj f31,f32,f121,f122
  f124: plane 19.05x2.03mm, normal (0.17,0,0.98), area 39.3mm2, adj f1,f31,f32,f126
  f125: plane 19.05x2.03mm, normal (0.17,0,-0.98), area 39.3mm2, adj f2,f31,f32,f126
  f126: plane 19.05x1.82mm, normal (1,0,0), area 34.7mm2, adj f31,f32,f124,f125
  f127: plane 19.05x2.03mm, normal (0.17,0,0.98), area 39.3mm2, adj f0,f31,f32,f129
  f128: plane 19.05x2.03mm, normal (0.17,0,-0.98), area 39.3mm2, adj f1,f31,f32,f129
  f129: plane 19.05x1.82mm, normal (1,0,0), area 34.7mm2, adj f31,f32,f127,f128
PART E: 8 faces, bbox 19.1x25.4x19.1 mm
  f0: plane 17.53x17.53mm, normal (0,-1,0), area 82.3mm2, adj f4,f5
  f1: plane 17.53x17.53mm, normal (0,1,0), area 82.3mm2, adj f6,f7
  f2: cylinder r=9.53mm len=23.88mm, axis (0,1,0), area 1428.9mm2, adj f4,f7
  f3: cylinder r=6.35mm len=23.88mm, axis (0,1,0), area 952.6mm2, adj f5,f6
  f4: cone r=9.53mm half-angle=45deg, axis (0,1,0), area 61.9mm2, adj f0,f2
  f5: cone r=6.35mm half-angle=45deg, axis (0,-1,0), area 45.6mm2, adj f0,f3
  f6: cone r=6.35mm half-angle=45deg, axis (0,1,0), area 45.6mm2, adj f1,f3
  f7: cone r=9.53mm half-angle=45deg, axis (0,-1,0), area 61.9mm2, adj f1,f2
PART F: 26 faces, bbox 12.7x44.5x63.5 mm
  f0: plane 63.5x12.7mm, normal (1,0,0), area 753.5mm2, adj f1,f2,f6,f7,f8,f14,f17,f25
  f1: cylinder r=6.35mm len=12.7mm, axis (1,0,0), area 126.7mm2, adj f0,f2,f8,f9
  f2: plane 31.75x12.7mm, normal (0,0,1), area 341.8mm2, adj f0,f1,f3,f9,f10,f23,f24,f25
  f3: cylinder r=6.35mm len=12.7mm, axis (1,0,0), area 126.7mm2, adj f2,f4,f9,f10
  f4: plane 50.8x12.7mm, normal (0,1,0), area 645.2mm2, adj f3,f5,f9,f10
  f5: cylinder r=6.35mm len=12.7mm, axis (1,0,0), area 126.7mm2, adj f4,f6,f9,f10
  f6: plane 31.75x12.7mm, normal (0,0,-1), area 341.8mm2, adj f0,f5,f7,f9,f10,f23,f24,f25
  f7: cylinder r=6.35mm len=12.7mm, axis (1,0,0), area 126.7mm2, adj f0,f6,f8,f9
  f8: plane 50.8x12.7mm, normal (0,-1,0), area 645.2mm2, adj f0,f1,f7,f9
  f9: plane 63.5x44.45mm, normal (-1,0,0), area 2502.9mm2, adj f1,f2,f3,f4,f5,f6,f7,f8
  f10: plane 63.5x12.7mm, normal (1,0,0), area 753.5mm2, adj f2,f3,f4,f5,f6,f11,f20,f24
  f11: cylinder r=2.38mm len=6.35mm, axis (-1,0,0), area 95mm2, adj f10,f12
  f12: plane 9.53x9.53mm, normal (-1,0,0), area 53.4mm2, adj f11,f13
  f13: cylinder r=4.76mm len=9.53mm, axis (-1,0,0), area 190mm2, adj f9,f12
  f14: cylinder r=2.38mm len=6.35mm, axis (-1,0,0), area 95mm2, adj f0,f15
  f15: plane 9.53x9.53mm, normal (-1,0,0), area 53.4mm2, adj f14,f16
  f16: cylinder r=4.76mm len=9.53mm, axis (-1,0,0), area 190mm2, adj f9,f15
  f17: cylinder r=2.38mm len=6.35mm, axis (-1,0,0), area 95mm2, adj f0,f18
  f18: plane 9.53x9.53mm, normal (-1,0,0), area 53.4mm2, adj f17,f19
  f19: cylinder r=4.76mm len=9.53mm, axis (-1,0,0), area 190mm2, adj f9,f18
  f20: cylinder r=2.38mm len=6.35mm, axis (-1,0,0), area 95mm2, adj f10,f21
  f21: plane 9.53x9.53mm, normal (-1,0,0), area 53.4mm2, adj f20,f22
  f22: cylinder r=4.76mm len=9.53mm, axis (-1,0,0), area 190mm2, adj f9,f21
  f23: plane 63.5x19.05mm, normal (1,0,0), area 1209.7mm2, adj f2,f6,f24,f25
  f24: plane 63.5x3.23mm, normal (0,-1,0), area 204.8mm2, adj f2,f6,f10,f23
  f25: plane 63.5x3.23mm, normal (0,1,0), area 204.8mm2, adj f0,f2,f6,f23
PLACE A t=(-0.76,3.17,0)mm
PLACE B rot(axis=(0,0,-1),90deg) t=(11.27,7,0)mm
PLACE C at identity fixed
PLACE D t=(6.35,19.05,0)mm
PLACE E t=(0,0.76,0)mm
PLACE F t=(6.35,0,0)mm
MATE fastened B.f18 <-> C.f6  axis (0,0,-1) through (10.66,0,-158.75)mm
